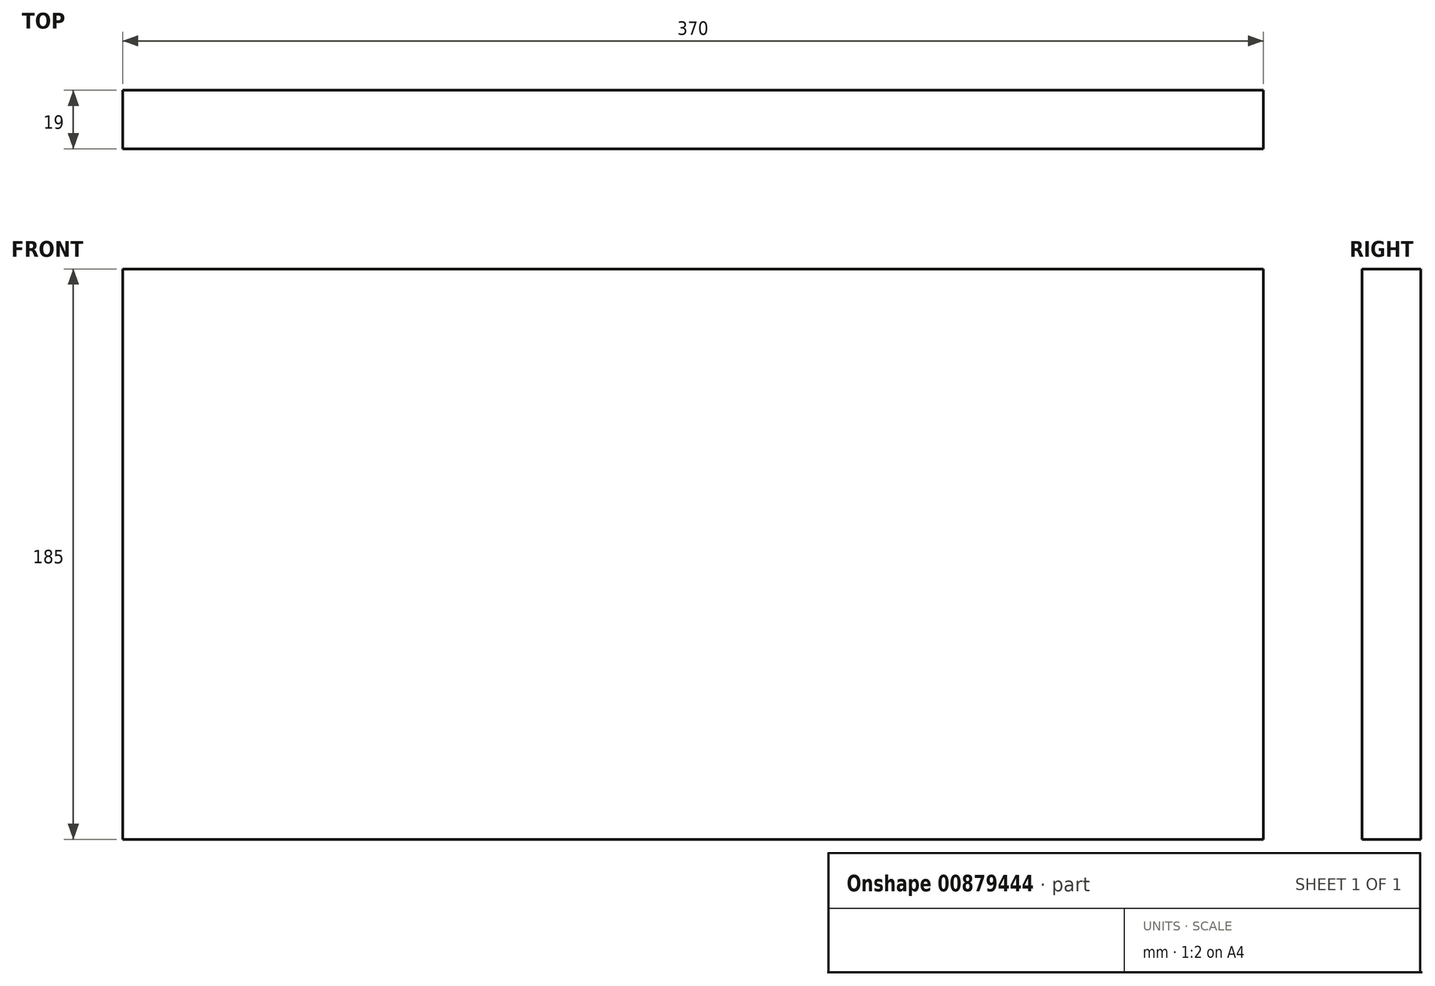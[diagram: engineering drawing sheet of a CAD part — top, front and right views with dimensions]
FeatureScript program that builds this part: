
annotation { "Feature Type Name" : "Feature", "Feature Type Description" : "" }
export const myFeature = defineFeature(function(context is Context, id is Id, definition is map)
    precondition{}
    {
        {
            var Q0;
            Q0=qCreatedBy(makeId("Front.planeOp"),FACE);
            var sketch = newSketch(context, id + "F0", { "sketchPlane" : qUnion([Q0])});
            skLineSegment(sketch, "E0.bottom", {"start": v(185, 92.5) * mm, "end": v(-185, 92.5) * mm});
            skLineSegment(sketch, "E0.top", {"start": v(185, -92.5) * mm, "end": v(-185, -92.5) * mm});
            skLineSegment(sketch, "E0.left", {"start": v(185, 92.5) * mm, "end": v(185, -92.5) * mm});
            skLineSegment(sketch, "E0.right", {"start": v(-185, 92.5) * mm, "end": v(-185, -92.5) * mm});
            skPoint(sketch, "E0.middle", {"position": v(0, 0) * mm});
            skSolve(sketch);
        }
        {
            var Q0;
            Q0=qSketchRegion(id+"F0",true);
            extrude(context, id + "F1", {"entities" : qUnion([Q0]), "flatOperationType" : FlatOperationType.REMOVE, "depth" : 19 * mm, "offsetDistance" : 25 * mm, "domain" : OperationDomain.MODEL});
        }
    });
